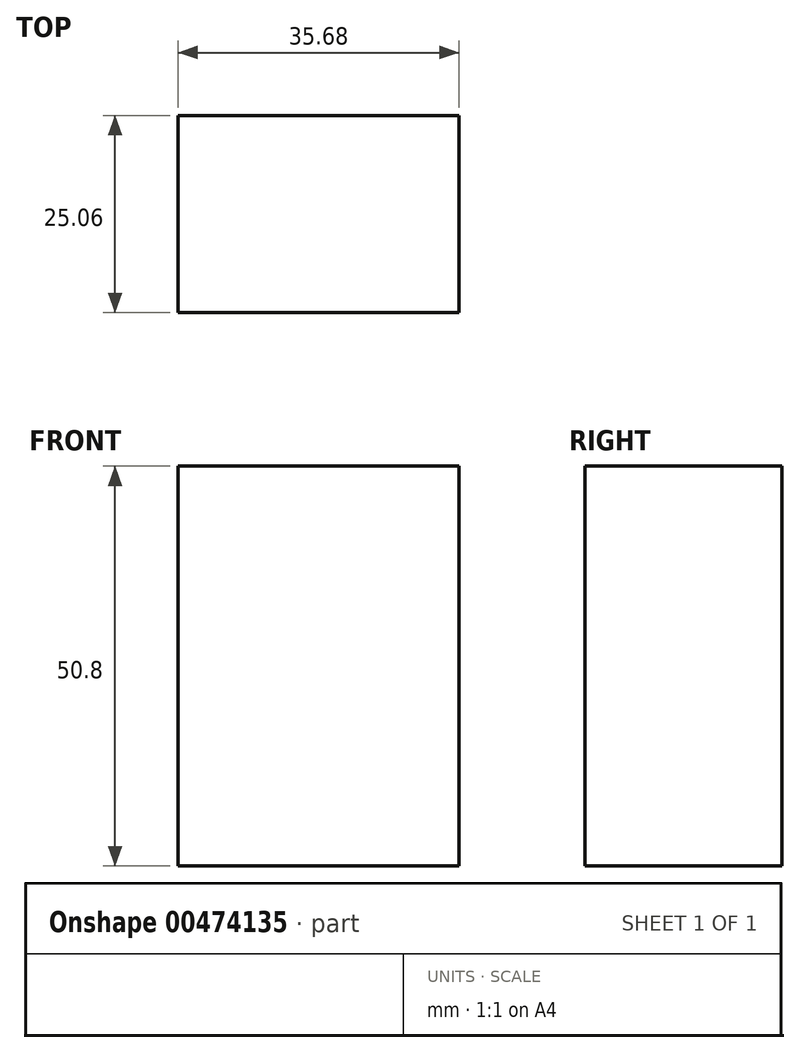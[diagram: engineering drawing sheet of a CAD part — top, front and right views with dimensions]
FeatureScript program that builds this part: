
annotation { "Feature Type Name" : "Feature", "Feature Type Description" : "" }
export const myFeature = defineFeature(function(context is Context, id is Id, definition is map)
    precondition{}
    {
        {
            var Q0;
            Q0=qCreatedBy(makeId("Top.planeOp"),FACE);
            var sketch = newSketch(context, id + "F0", { "sketchPlane" : qUnion([Q0])});
            skLineSegment(sketch, "E0.bottom", {"start": v(17.84, -12.53) * mm, "end": v(-17.84, -12.53) * mm});
            skLineSegment(sketch, "E0.top", {"start": v(17.84, 12.53) * mm, "end": v(-17.84, 12.53) * mm});
            skLineSegment(sketch, "E0.left", {"start": v(17.84, -12.53) * mm, "end": v(17.84, 12.53) * mm});
            skLineSegment(sketch, "E0.right", {"start": v(-17.84, -12.53) * mm, "end": v(-17.84, 12.53) * mm});
            skPoint(sketch, "E0.middle", {"position": v(0, 0) * mm});
            skSolve(sketch);
        }
        {
            var Q0;
            Q0=makeQuery(id+"F0.imprint","IMPRINT",FACE,{"disambiguationData":[TD([[makeQuery(id+"F0.imprint","IMPRINT",EDGE,{"derivedFrom":sQuery(id+"F0.wireOp",EDGE,"E0.bottom")}),-1.0]])]});
            extrude(context, id + "F1", {"entities" : qUnion([Q0]), "depth" : 50.8 * mm});
        }
    });
